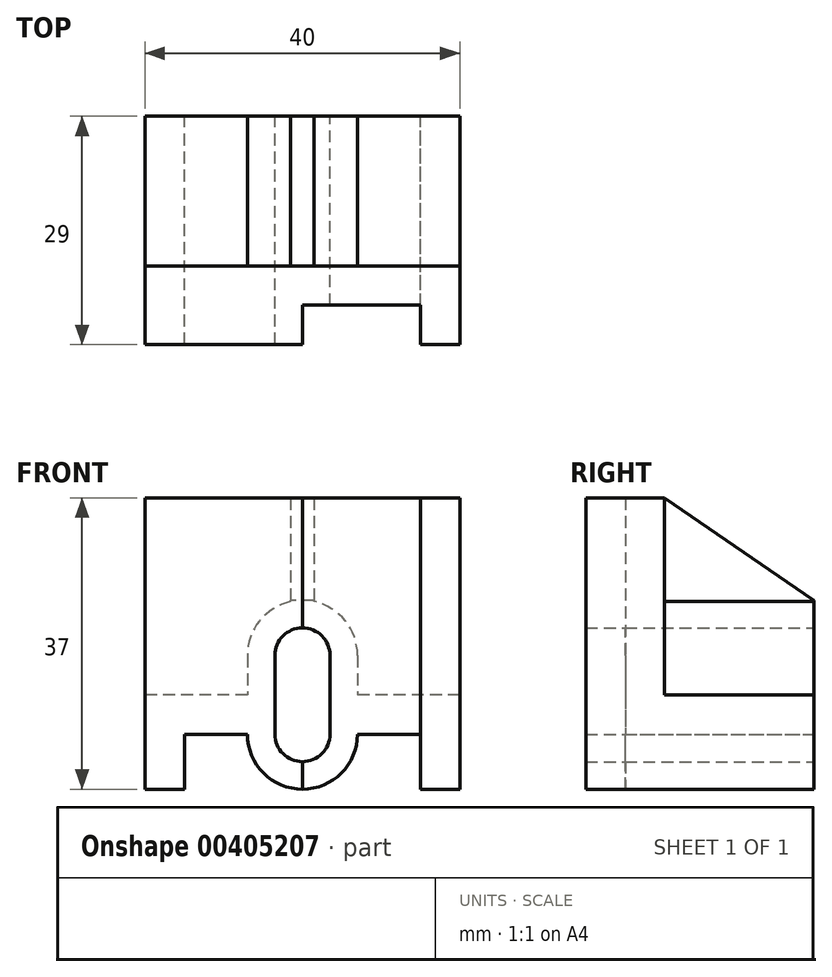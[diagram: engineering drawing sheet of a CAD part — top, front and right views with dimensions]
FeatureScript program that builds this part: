
annotation { "Feature Type Name" : "Feature", "Feature Type Description" : "" }
export const myFeature = defineFeature(function(context is Context, id is Id, definition is map)
    precondition{}
    {
        {
            var Q0;
            Q0=qCreatedBy(makeId("Front.planeOp"),FACE);
            var sketch = newSketch(context, id + "F0", { "sketchPlane" : qUnion([Q0])});
            skArc(sketch, "E0", {"start": v(-3.5, 0) * mm, "mid": v(0, -3.5) * mm, "end": v(3.5, 0) * mm});
            skLineSegment(sketch, "E1", {"start": v(0, 0) * mm, "end": v(3.5, 0) * mm, "construction": true});
            skLineSegment(sketch, "E2", {"start": v(0, 0) * mm, "end": v(15, 0) * mm});
            skLineSegment(sketch, "E3", {"start": v(0, 0) * mm, "end": v(-15, 0) * mm});
            skLineSegment(sketch, "E4", {"start": v(-15, 0) * mm, "end": v(-15, -7) * mm});
            skLineSegment(sketch, "E5", {"start": v(-15, -7) * mm, "end": v(-20, -7) * mm});
            skLineSegment(sketch, "E6", {"start": v(15, 0) * mm, "end": v(15, -7) * mm});
            skLineSegment(sketch, "E7", {"start": v(15, -7) * mm, "end": v(20, -7) * mm});
            skLineSegment(sketch, "E8", {"start": v(0, 0) * mm, "end": v(0, 41.6) * mm, "construction": true});
            skLineSegment(sketch, "E9", {"start": v(-3.5, 0) * mm, "end": v(-3.5, 10) * mm});
            skLineSegment(sketch, "E10", {"start": v(3.5, 0) * mm, "end": v(3.5, 10) * mm});
            skLineSegment(sketch, "E11", {"start": v(-3.5, 10) * mm, "end": v(3.5, 10) * mm, "construction": true});
            skArc(sketch, "E12", {"start": v(3.5, 10) * mm, "mid": v(0, 13.5) * mm, "end": v(-3.5, 10) * mm});
            skArc(sketch, "E13", {"start": v(-7, 0) * mm, "mid": v(0, -7) * mm, "end": v(7, 0) * mm});
            skLineSegment(sketch, "E14", {"start": v(-7, 0) * mm, "end": v(7, 0) * mm, "construction": true});
            skPoint(sketch, "E14.startSnap0", {"position": v(-7.5, 0) * mm});
            skArc(sketch, "E15", {"start": v(7, 10) * mm, "mid": v(0, 17) * mm, "end": v(-7, 10) * mm});
            skLineSegment(sketch, "E16", {"start": v(-7, 10) * mm, "end": v(7, 10) * mm, "construction": true});
            skLineSegment(sketch, "E17", {"start": v(20, -7) * mm, "end": v(20, 5) * mm});
            skLineSegment(sketch, "E18", {"start": v(-20, -7) * mm, "end": v(-20, 5) * mm});
            skLineSegment(sketch, "E19", {"start": v(20, 5) * mm, "end": v(7, 5) * mm});
            skLineSegment(sketch, "E20", {"start": v(-7, 10) * mm, "end": v(-7, 5) * mm});
            skLineSegment(sketch, "E21", {"start": v(7, 10) * mm, "end": v(7, 5) * mm});
            skLineSegment(sketch, "E22.trimOffspring", {"start": v(-7, 5) * mm, "end": v(-20, 5) * mm});
            skSolve(sketch);
        }
        {
            var Q0;
            {var subQ3=sQuery(id+"F0.wireOp",EDGE,"E4");Q0=makeQuery(id+"F0.imprint","IMPRINT",FACE,{"disambiguationData":[TD([[makeQuery(id+"F0.imprint","IMPRINT",EDGE,{"derivedFrom":subQ3}),-1.0]])]});}
            var Q1;
            {var subQ0=sQuery(id+"F0.wireOp",EDGE,"E0");Q1=makeQuery(id+"F0.imprint","IMPRINT",FACE,{"disambiguationData":[TD([[makeQuery(id+"F0.imprint","IMPRINT",EDGE,{"derivedFrom":subQ0}),-1.0]])]});}
            extrude(context, id + "F1", {"entities" : qUnion([Q0, Q1]), "depth" : 19 * mm});
        }
        {
            var Q0;
            Q0=qCreatedBy(makeId("Right.planeOp"),FACE);
            var sketch = newSketch(context, id + "F2", { "sketchPlane" : qUnion([Q0])});
            skPoint(sketch, "E23.0", {"position": v(0, -7) * mm});
            skPoint(sketch, "E24.0", {"position": v(-19, -7) * mm});
            skPoint(sketch, "E25.0", {"position": v(0, 0) * mm});
            skLineSegment(sketch, "E26", {"start": v(-19, -7) * mm, "end": v(-29, -7) * mm});
            skLineSegment(sketch, "E27", {"start": v(-29, -7) * mm, "end": v(-29, 30) * mm});
            skLineSegment(sketch, "E28", {"start": v(-29, 30) * mm, "end": v(-19, 30) * mm});
            skLineSegment(sketch, "E29", {"start": v(-19, 30) * mm, "end": v(-19, 17) * mm});
            skLineSegment(sketch, "E30", {"start": v(-19, 17) * mm, "end": v(-19, -7) * mm});
            skSolve(sketch);
        }
        {
            var Q0;
            Q0=makeQuery(id+"F2.imprint","IMPRINT",FACE,{"disambiguationData":[TD([[makeQuery(id+"F2.imprint","IMPRINT",EDGE,{"derivedFrom":sQuery(id+"F2.wireOp",EDGE,"E26")}),-1.0]])]});
            extrude(context, id + "F3", {"entities" : qUnion([Q0]), "operationType" : NewBodyOperationType.ADD, "endBound" : BoundingType.SYMMETRIC, "depth" : 40 * mm});
        }
        {
            var Q0;
            Q0=qCreatedBy(makeId("Right.planeOp"),FACE);
            var sketch = newSketch(context, id + "F4", { "sketchPlane" : qUnion([Q0])});
            skLineSegment(sketch, "E31.0", {"start": v(-29, 30) * mm, "end": v(-19, 30) * mm});
            skLineSegment(sketch, "E32.0", {"start": v(-19, 30) * mm, "end": v(-19, 17) * mm});
            skLineSegment(sketch, "E33", {"start": v(-19, 17) * mm, "end": v(0, 17) * mm});
            skLineSegment(sketch, "E34.0", {"start": v(0, 10) * mm, "end": v(0, 17) * mm});
            skLineSegment(sketch, "E35", {"start": v(-19, 30) * mm, "end": v(0, 17) * mm});
            skSolve(sketch);
        }
        {
            var Q0;
            Q0=makeQuery(id+"F4.imprint","IMPRINT",FACE,{"disambiguationData":[TD([[makeQuery(id+"F4.imprint","IMPRINT",EDGE,{"derivedFrom":sQuery(id+"F4.wireOp",EDGE,"E32.0")}),1.0]])]});
            extrude(context, id + "F5", {"entities" : qUnion([Q0]), "endBound" : BoundingType.SYMMETRIC, "depth" : 3 * mm});
        }
        {
            var Q0;
            Q0=qCreatedBy(makeId("Top.planeOp"),FACE);
            var sketch = newSketch(context, id + "F6", { "sketchPlane" : qUnion([Q0])});
            skLineSegment(sketch, "E36.0", {"start": v(20, -29) * mm, "end": v(20, -19) * mm});
            skLineSegment(sketch, "E37.0", {"start": v(20, -29) * mm, "end": v(-20, -29) * mm});
            skLineSegment(sketch, "E38.0", {"start": v(20, -19) * mm, "end": v(-20, -19) * mm});
            skLineSegment(sketch, "E39.0", {"start": v(0, -29) * mm, "end": v(0, -19) * mm});
            skLineSegment(sketch, "E40", {"start": v(20, -29) * mm, "end": v(15, -29) * mm});
            skLineSegment(sketch, "E41", {"start": v(20, -29) * mm, "end": v(20, -24) * mm});
            skLineSegment(sketch, "E42", {"start": v(15, -29) * mm, "end": v(15, -24) * mm});
            skLineSegment(sketch, "E43", {"start": v(0, -29) * mm, "end": v(0, -24) * mm});
            skLineSegment(sketch, "E44", {"start": v(15, -24) * mm, "end": v(0, -24) * mm});
            skSolve(sketch);
        }
        {
            var Q0;
            {var subQ0=sQuery(id+"F6.wireOp",EDGE,"E42");Q0=makeQuery(id+"F6.imprint","IMPRINT",FACE,{"disambiguationData":[TD([[makeQuery(id+"F6.imprint","IMPRINT",EDGE,{"derivedFrom":subQ0}),1.0]])]});}
            extrude(context, id + "F7", {"entities" : qUnion([Q0]), "operationType" : NewBodyOperationType.REMOVE, "endBound" : BoundingType.THROUGH_ALL, "depth" : 25 * mm});
        }
        {
            var Q0;
            {var subQ0=sQuery(id+"F6.wireOp",EDGE,"E44");var subQ1=sQuery(id+"F6.wireOp",EDGE,"E43");var subQ2=sQuery(id+"F6.wireOp",EDGE,"E42");var subQ3=sQuery(id+"F6.wireOp",EDGE,"E37.0");Q0=makeQuery(id+"FYAVn50JzPeO8gW_2.1.F7.boolean.opBoolean","MERGE",FACE,{"derivedFrom":[makeQuery(id+"F7.boolean.opBoolean","COPY",FACE,{"derivedFrom":makeQuery(id+"F7.opExtrude","CAP_FACE",FACE,{"disambiguationData":[OSD([subQ3,subQ2,subQ1,subQ0])],"isStart":true})}),makeQuery(id+"FYAVn50JzPeO8gW_2.1.F7.opExtrude","CAP_FACE",FACE,{"disambiguationData":[OSD([subQ3,subQ2,subQ1,subQ0])],"isStart":true})]});}
            extrude(context, id + "F8", {"entities" : qUnion([Q0]), "operationType" : NewBodyOperationType.REMOVE, "oppositeDirection" : true, "depth" : 25 * mm});
        }
        {
            var Q0;
            {var subQ0=makeQuery(id+"F3.opExtrude","SWEPT_FACE",FACE,{"disambiguationData":[OSD([sQuery(id+"F2.wireOp",EDGE,"E29"),sQuery(id+"F2.wireOp",EDGE,"E30")])]});Q0=makeQuery(id+"F3.boolean.opBoolean","SPLIT",FACE,{"disambiguationData":[TD([makeQuery(id+"F1.opExtrude","SWEPT_FACE",FACE,{"disambiguationData":[OSD([sQuery(id+"F0.wireOp",EDGE,"E3")])]})])],"derivedFrom":subQ0});}
            var Q1;
            {var subQ0=makeQuery(id+"F3.opExtrude","SWEPT_FACE",FACE,{"disambiguationData":[OSD([sQuery(id+"F2.wireOp",EDGE,"E29"),sQuery(id+"F2.wireOp",EDGE,"E30")])]});Q1=makeQuery(id+"F3.boolean.opBoolean","SPLIT",FACE,{"disambiguationData":[TD([makeQuery(id+"F1.opExtrude","SWEPT_FACE",FACE,{"disambiguationData":[OSD([sQuery(id+"F0.wireOp",EDGE,"E2")])]})])],"derivedFrom":subQ0});}
            var Q2;
            Q2=makeQuery(id+"F3.boolean.opBoolean","SPLIT",FACE,{"disambiguationData":[TD([makeQuery(id+"F1.opExtrude","SWEPT_FACE",FACE,{"disambiguationData":[OSD([sQuery(id+"F0.wireOp",EDGE,"E0")])]})])],"derivedFrom":makeQuery(id+"F3.opExtrude","SWEPT_FACE",FACE,{"disambiguationData":[OSD([sQuery(id+"F2.wireOp",EDGE,"E29"),sQuery(id+"F2.wireOp",EDGE,"E30")])]})});
            extrude(context, id + "F9", {"entities" : qUnion([Q0, Q1, Q2]), "operationType" : NewBodyOperationType.REMOVE, "oppositeDirection" : true, "depth" : 25 * mm});
        }
        {
            var Q0;
            Q0=makeQuery(id+"F5.opExtrude","SWEPT_FACE",FACE,{"disambiguationData":[OSD([sQuery(id+"F4.wireOp",EDGE,"E33")])]});
            extrude(context, id + "F10", {"entities" : qUnion([Q0]), "operationType" : NewBodyOperationType.ADD, "endBound" : BoundingType.UP_TO_NEXT, "depth" : 25 * mm});
        }
    });
